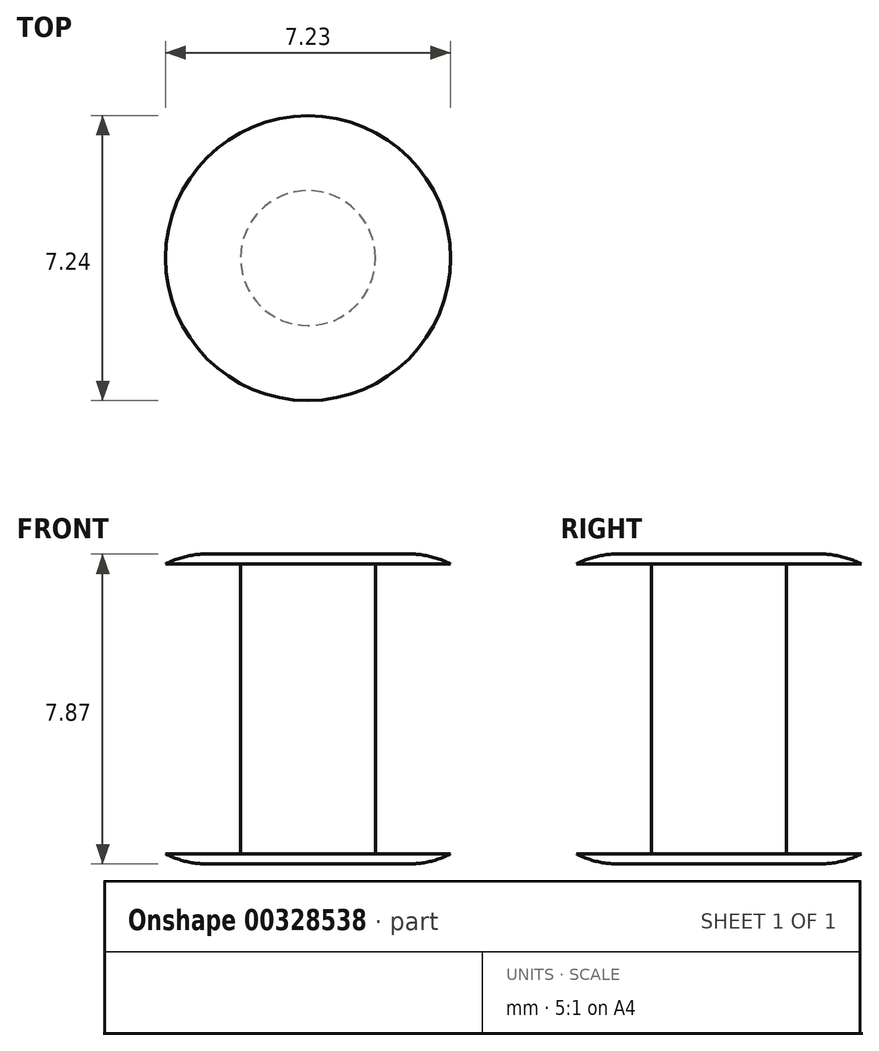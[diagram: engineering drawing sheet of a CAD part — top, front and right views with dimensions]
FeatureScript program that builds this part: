
annotation { "Feature Type Name" : "Feature", "Feature Type Description" : "" }
export const myFeature = defineFeature(function(context is Context, id is Id, definition is map)
    precondition{}
    {
        {
            var Q0;
            Q0=qCreatedBy(makeId("Front.planeOp"),FACE);
            var sketch = newSketch(context, id + "F0", { "sketchPlane" : qUnion([Q0])});
            skLineSegment(sketch, "E0", {"start": v(-30.48, 20.57) * mm, "end": v(-28.58, 20.57) * mm});
            skLineSegment(sketch, "E1", {"start": v(-28.58, 20.57) * mm, "end": v(-28.58, 20.32) * mm});
            skLineSegment(sketch, "E2", {"start": v(-28.58, 20.32) * mm, "end": v(-30.48, 20.32) * mm});
            skLineSegment(sketch, "E3", {"start": v(-30.48, 20.32) * mm, "end": v(-30.48, 12.95) * mm});
            skLineSegment(sketch, "E4", {"start": v(-30.48, 12.95) * mm, "end": v(-28.58, 12.95) * mm});
            skLineSegment(sketch, "E5", {"start": v(-28.58, 12.95) * mm, "end": v(-28.58, 12.7) * mm});
            skLineSegment(sketch, "E6", {"start": v(-28.58, 12.7) * mm, "end": v(-30.48, 12.7) * mm});
            skLineSegment(sketch, "E7", {"start": v(-30.48, 20.57) * mm, "end": v(-30.48, 20.32) * mm});
            skLineSegment(sketch, "E8", {"start": v(-30.48, 12.7) * mm, "end": v(-30.48, 12.95) * mm});
            skLineSegment(sketch, "E9", {"start": v(-30.48, 12.7) * mm, "end": v(-32.2, 12.7) * mm});
            skLineSegment(sketch, "E10", {"start": v(-32.2, 12.7) * mm, "end": v(-32.2, 20.57) * mm});
            skLineSegment(sketch, "E11", {"start": v(-32.2, 20.57) * mm, "end": v(-30.48, 20.57) * mm});
            skSolve(sketch);
        }
        {
            var Q0;
            Q0 = qSketchRegion(id + "F0", true);
            var Q1;
            Q1=sQuery(id+"F0.wireOp",EDGE,"E10");
            revolve(context, id + "F1", {"entities" : qUnion([Q0]), "axis" : qUnion([Q1]), "revolveType" : RevolveType.FULL});
        }
        {
            var Q0;
            Q0=makeQuery(id+"F1.opRevolve","SWEPT_FACE",FACE,{"disambiguationData":[OSD([sQuery(id+"F0.wireOp",EDGE,"E0"),sQuery(id+"F0.wireOp",EDGE,"E11")])]});
            fillet(context, id + "F2", {"entities" : qUnion([Q0]), "radius" : 2.3 * mm, "tangentPropagation" : true, "allowEdgeOverflow" : false});
        }
        {
            var Q0;
            Q0=makeQuery(id+"F1.opRevolve","SWEPT_EDGE",EDGE,{"disambiguationData":[OSD([sQuery(id+"F0.wireOp",EDGE,"E5"),sQuery(id+"F0.wireOp",EDGE,"E6")])]});
            fillet(context, id + "F3", {"entities" : qUnion([Q0]), "radius" : 2.3 * mm, "tangentPropagation" : true, "allowEdgeOverflow" : false});
        }
    });
